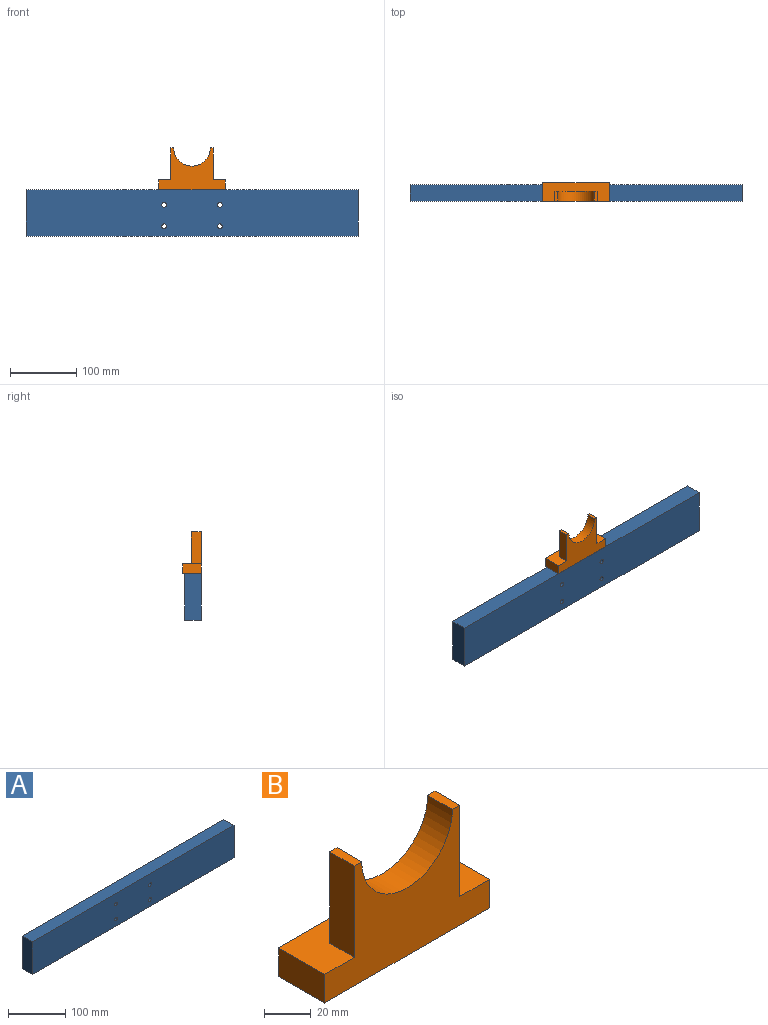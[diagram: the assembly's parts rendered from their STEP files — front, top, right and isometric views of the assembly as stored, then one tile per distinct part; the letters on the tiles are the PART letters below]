
ASSEMBLY  parts=2 mates=1
PART A: 10 faces, bbox 500x25x70 mm
  f0: plane 500x25mm, normal (0,0,-1), area 12500mm2, adj f1,f3,f4,f5
  f1: plane 500x70mm, normal (0,1,0), area 34846.1mm2, adj f0,f2,f4,f5,f6,f7,f8,f9
  f2: plane 500x25mm, normal (0,0,1), area 12500mm2, adj f1,f3,f4,f5
  f3: plane 500x70mm, normal (0,-1,0), area 34846.1mm2, adj f0,f2,f4,f5,f6,f7,f8,f9
  f4: plane 70x25mm, normal (1,0,0), area 1750mm2, adj f0,f1,f2,f3
  f5: plane 70x25mm, normal (-1,0,0), area 1750mm2, adj f0,f1,f2,f3
  f6: cylinder r=3.5mm len=25mm, axis (0,-1,0), area 549.8mm2, adj f1,f3
  f7: cylinder r=3.5mm len=25mm, axis (0,-1,0), area 549.8mm2, adj f1,f3
  f8: cylinder r=3.5mm len=25mm, axis (0,-1,0), area 549.8mm2, adj f1,f3
  f9: cylinder r=3.5mm len=25mm, axis (0,-1,0), area 549.8mm2, adj f1,f3
PART B: 12 faces, bbox 100x28x63 mm
  f0: plane 100x15mm, normal (0,1,0), area 1500mm2, adj f2,f3,f4,f5
  f1: plane 48x15mm, normal (-1,0,0), area 720mm2, adj f5,f7,f8,f9
  f2: plane 28x15mm, normal (-1,0,0), area 420mm2, adj f0,f3,f5,f7
  f3: plane 100x28mm, normal (0,0,-1), area 2800mm2, adj f0,f2,f4,f7
  f4: plane 28x15mm, normal (1,0,0), area 420mm2, adj f0,f3,f5,f7
  f5: plane 100x28mm, normal (0,0,1), area 1840mm2, adj f0,f1,f2,f4,f6,f7,f8
  f6: plane 48x15mm, normal (1,0,0), area 720mm2, adj f5,f7,f8,f11
  f7: plane 100x63mm, normal (0,-1,0), area 3384.1mm2, adj f1,f2,f3,f4,f5,f6,f9,f10
  f8: plane 64x48mm, normal (0,1,0), area 1884.1mm2, adj f1,f5,f6,f9,f10,f11
  f9: plane 15x4.5mm, normal (0,0,1), area 67.5mm2, adj f1,f7,f8,f10
  f10: cylinder r=27.5mm len=55mm, axis (0,-1,0), area 1295.9mm2, adj f7,f8,f9,f11
  f11: plane 15x4.5mm, normal (0,0,1), area 67.5mm2, adj f6,f7,f8,f10
PLACE A t=(3.17,0.49,-2.02)mm fixed
PLACE B t=(3.17,15.99,40.48)mm
MATE fastened A.f2 <-> B.f3  axis (0,0,1) through (3.17,-12.01,32.98)mm
